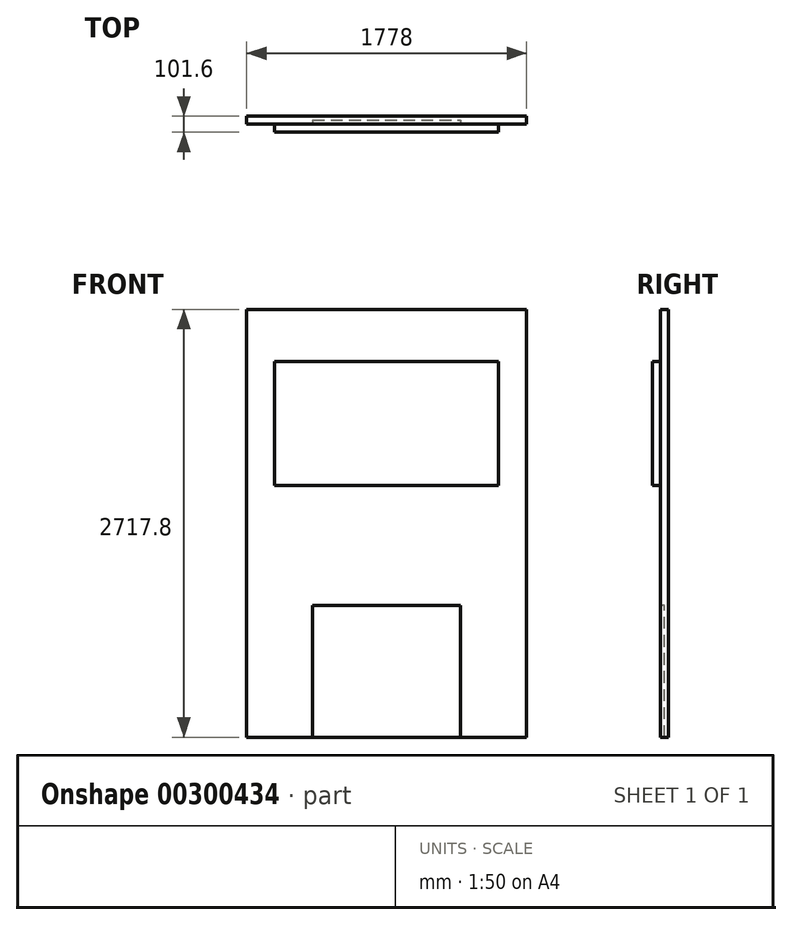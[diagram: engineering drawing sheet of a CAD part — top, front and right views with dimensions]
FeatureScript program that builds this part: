
annotation { "Feature Type Name" : "Feature", "Feature Type Description" : "" }
export const myFeature = defineFeature(function(context is Context, id is Id, definition is map)
    precondition{}
    {
        {
            var Q0;
            Q0=qCreatedBy(makeId("Front.planeOp"),FACE);
            var sketch = newSketch(context, id + "F0", { "sketchPlane" : qUnion([Q0])});
            skLineSegment(sketch, "E0.bottom", {"start": v(-889, 1003.3) * mm, "end": v(889, 1003.3) * mm});
            skLineSegment(sketch, "E0.top", {"start": v(-889, -1714.5) * mm, "end": v(889, -1714.5) * mm});
            skLineSegment(sketch, "E0.left", {"start": v(-889, 1003.3) * mm, "end": v(-889, -1714.5) * mm});
            skLineSegment(sketch, "E0.right", {"start": v(889, 1003.3) * mm, "end": v(889, -1714.5) * mm});
            skSolve(sketch);
        }
        {
            var Q0;
            Q0=makeQuery(id+"F0.imprint","IMPRINT",FACE,{"disambiguationData":[TD([[makeQuery(id+"F0.imprint","IMPRINT",EDGE,{"derivedFrom":sQuery(id+"F0.wireOp",EDGE,"E0.bottom")}),-1.0]])]});
            extrude(context, id + "F1", {"entities" : qUnion([Q0]), "depth" : 50.8 * mm});
        }
        {
            var Q0;
            Q0=makeQuery(id+"F1.opExtrude","CAP_FACE",FACE,{"disambiguationData":[OSD([sQuery(id+"F0.wireOp",EDGE,"E0.bottom"),sQuery(id+"F0.wireOp",EDGE,"E0.top"),sQuery(id+"F0.wireOp",EDGE,"E0.left"),sQuery(id+"F0.wireOp",EDGE,"E0.right")])],"isStart":false});
            var sketch = newSketch(context, id + "F2", { "sketchPlane" : qUnion([Q0])});
            skLineSegment(sketch, "E1", {"start": v(-469.9, -1714.5) * mm, "end": v(-469.9, -876.3) * mm});
            skLineSegment(sketch, "E2", {"start": v(-469.9, -876.3) * mm, "end": v(469.9, -876.3) * mm});
            skLineSegment(sketch, "E3", {"start": v(469.9, -876.3) * mm, "end": v(469.9, -1714.5) * mm});
            skLineSegment(sketch, "E4", {"start": v(469.9, -1714.5) * mm, "end": v(-469.9, -1714.5) * mm});
            skSolve(sketch);
        }
        {
            var Q0;
            Q0=makeQuery(id+"F2.imprint","IMPRINT",FACE,{"disambiguationData":[TD([[makeQuery(id+"F2.imprint","IMPRINT",EDGE,{"derivedFrom":sQuery(id+"F2.wireOp",EDGE,"E1")}),-1.0]])]});
            extrude(context, id + "F3", {"entities" : qUnion([Q0]), "operationType" : NewBodyOperationType.REMOVE, "oppositeDirection" : true, "depth" : 25.4 * mm});
        }
        {
            var Q0;
            {var subQ1=sQuery(id+"F2.wireOp",EDGE,"E1");Q0=makeQuery(id+"F2.imprint","IMPRINT",FACE,{"disambiguationData":[TD([[makeQuery(id+"F2.imprint","IMPRINT",EDGE,{"derivedFrom":subQ1}),1.0]])]});}
            var sketch = newSketch(context, id + "F4", { "sketchPlane" : qUnion([Q0])});
            skLineSegment(sketch, "E5.bottom", {"start": v(-711.2, 673.1) * mm, "end": v(711.2, 673.1) * mm});
            skLineSegment(sketch, "E5.top", {"start": v(-711.2, -114.3) * mm, "end": v(711.2, -114.3) * mm});
            skLineSegment(sketch, "E5.left", {"start": v(-711.2, 673.1) * mm, "end": v(-711.2, -114.3) * mm});
            skLineSegment(sketch, "E5.right", {"start": v(711.2, 673.1) * mm, "end": v(711.2, -114.3) * mm});
            skSolve(sketch);
        }
        {
            var Q0;
            Q0=qSketchRegion(id+"F4",true);
            var Q1;
            Q1=qConstructionFilter(qBodyType(qCreatedBy(id+"F4",EDGE),BodyType.WIRE),ConstructionObject.NO);
            extrude(context, id + "F5", {"entities" : qUnion([Q0]), "operationType" : NewBodyOperationType.ADD, "surfaceEntities" : qUnion([Q1]), "depth" : 50.8 * mm});
        }
    });
